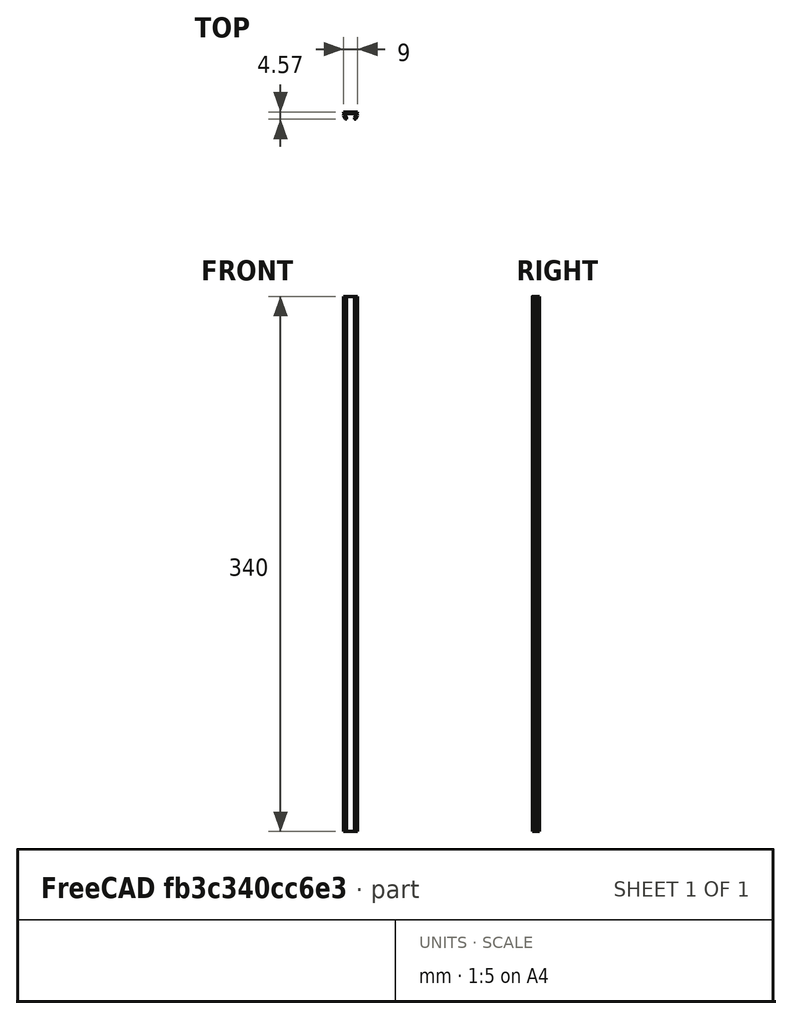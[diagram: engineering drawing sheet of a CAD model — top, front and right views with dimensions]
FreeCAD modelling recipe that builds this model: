
FCSTD DOCUMENT  (FreeCAD 0.17R13387 (Git))
Label: Strip_finishing_channel_8_X
License: All rights reserved
LicenseURL: http://en.wikipedia.org/wiki/All_rights_reserved
objects: Sketcher::SketchObject×1, PartDesign::Pad×1, PartDesign::Body×1
note: 4 computed .brp shape members not serialized (recipe doc carries the construction recipe); baked Part::Feature solids carry a one-line shape summary decoded from their .brp

FEATURE [Sketcher::SketchObject] Sketch
  MapMode = 5
  Support = -> [XY_Plane]
  sketch-geometry (16):
    g0: LineSegment StartX=-4.5 StartY=4.3 StartZ=0 EndX=4.5 EndY=4.3 EndZ=0
    g1: LineSegment StartX=4.5 StartY=4.3 StartZ=0 EndX=4.5 EndY=4 EndZ=0
    g2: LineSegment StartX=4.5 StartY=4 StartZ=0 EndX=3.9 EndY=4 EndZ=0
    g3: LineSegment StartX=3.9 StartY=4 StartZ=0 EndX=4.5 EndY=2 EndZ=0
    g4: LineSegment StartX=4.5 StartY=2 StartZ=0 EndX=3.44197 EndY=0 EndZ=0
    g5: LineSegment StartX=2.55803 StartY=0.467615 StartZ=0 EndX=3.36869 EndY=2 EndZ=0
    g6: LineSegment StartX=3.36869 StartY=2 StartZ=0 EndX=3 EndY=3.22897 EndZ=0
    g7: LineSegment StartX=-3 StartY=3.22897 StartZ=0 EndX=-3.36869 EndY=2 EndZ=0
    g8: LineSegment StartX=-3.36869 StartY=2 StartZ=0 EndX=-2.55803 EndY=0.467615 EndZ=0
    g9: LineSegment StartX=-3.44197 StartY=0 StartZ=0 EndX=-4.5 EndY=2 EndZ=0
    g10: LineSegment StartX=-4.5 StartY=2 StartZ=0 EndX=-3.9 EndY=4 EndZ=0
    g11: LineSegment StartX=-3.9 StartY=4 StartZ=0 EndX=-4.5 EndY=4 EndZ=0
    g12: LineSegment StartX=-4.5 StartY=4 StartZ=0 EndX=-4.5 EndY=4.3 EndZ=0
    g13: ArcOfCircle CenterX=-3 CenterY=0.233808 CenterZ=0 NormalX=0 NormalY=0 NormalZ=1 AngleXU=0 Radius=0.5 StartAngle=3.62818 EndAngle=6.76978
    g14: ArcOfCircle CenterX=3 CenterY=0.233808 CenterZ=0 NormalX=0 NormalY=0 NormalZ=1 AngleXU=0 Radius=0.5 StartAngle=2.655 EndAngle=5.79659
    g15: LineSegment StartX=-3 StartY=3.22897 StartZ=0 EndX=3 EndY=3.22897 EndZ=0
  constraints (46):
    c: Coincident(g0,g1)
    c: Coincident(g1,g2)
    c: Coincident(g2,g3)
    c: Coincident(g7,g8)
    c: Coincident(g9,g10)
    c: Coincident(g10,g11)
    c: Horizontal(g11)
    c: Coincident(g11,g12)
    c: Coincident(g12,g0)
    c: DistanceX(g0,g0) = 9
    c: Vertical(g12)
    c: Vertical(g1)
    c: Horizontal(g2)
    c: DistanceY(g12,g12) = 0.3
    c: Equal(g12,g1)
    c: Equal(g11,g2)
    c: Symmetric(g0,g0,g-2)
    c: Equal(g9,g4)
    c: Equal(g5,g8)
    c: Parallel(g9,g8)
    c: Parallel(g5,g4)
    c: DistanceX(g2,g2) = 0.6
    c: Coincident(g6,g5)
    c: Coincident(g4,g3)
    c: PointOnObject(g4,g-1)
    c: PointOnObject(g9,g-1)
    c: Symmetric(g9,g4,g-2)
    c: DistanceX(g9,g3) = 9
    c: DistanceY(g0) = 4.3
    c: DistanceY(g3) = 2
    c: Tangent(g13,g8) = 1.5708
    c: Tangent(g13,g9) = 1.5708
    c: Tangent(g14,g4) = 1.5708
    c: Tangent(g14,g5) = 1.5708
    c: Radius(g13) = 0.5
    c: Equal(g13,g14)
    c: Coincident(g15,g7)
    c: Coincident(g15,g6)
    c: Horizontal(g15)
    c: Symmetric(g7,g6,g-2)
    c: Parallel(g10,g7)
    c: Parallel(g6,g3)
    c: DistanceX(g15,g15) = 6
    c: Equal(g7,g6)
    c: DistanceX(g13,g14) = 6
    c: DistanceY(g5) = 2
FEATURE [PartDesign::Pad] Pad
  Length = 340
  Length2 = 100
  Profile = -> Sketch
  Type = 0
FEATURE [PartDesign::Body] Body
  Group = -> [Sketch,Pad]
  Origin = -> Origin
  Tip = -> Pad
